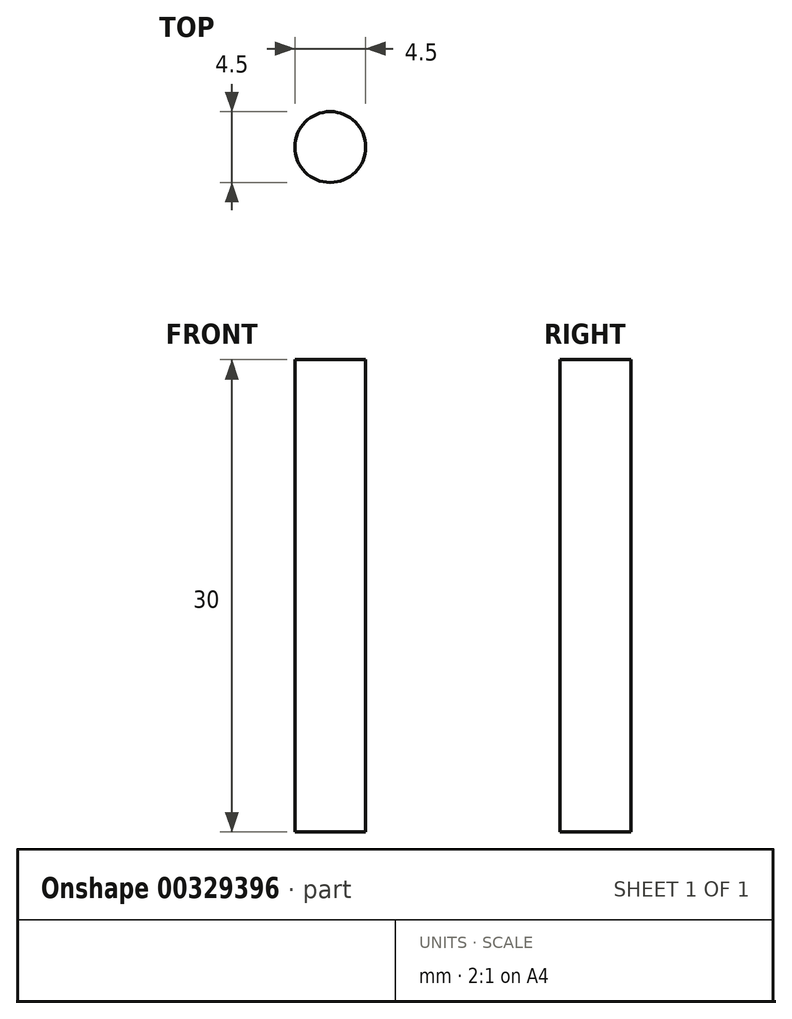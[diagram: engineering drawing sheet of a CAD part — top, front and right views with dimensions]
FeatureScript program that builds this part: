
annotation { "Feature Type Name" : "Feature", "Feature Type Description" : "" }
export const myFeature = defineFeature(function(context is Context, id is Id, definition is map)
    precondition{}
    {
        {
            var Q0;
            Q0=qCreatedBy(makeId("Top.planeOp"),FACE);
            var sketch = newSketch(context, id + "F0", { "sketchPlane" : qUnion([Q0])});
            skCircle(sketch, "E0", {"center": v(0, 0) * mm, "radius": 2.25 * mm});
            skSolve(sketch);
        }
        {
            var Q0;
            Q0=makeQuery(id+"F0.imprint","IMPRINT",FACE,{"disambiguationData":[TD([[makeQuery(id+"F0.imprint","IMPRINT",EDGE,{"derivedFrom":sQuery(id+"F0.wireOp",EDGE,"E0")}),1.0]])]});
            extrude(context, id + "F1", {"entities" : qUnion([Q0]), "depth" : 30 * mm});
        }
    });
